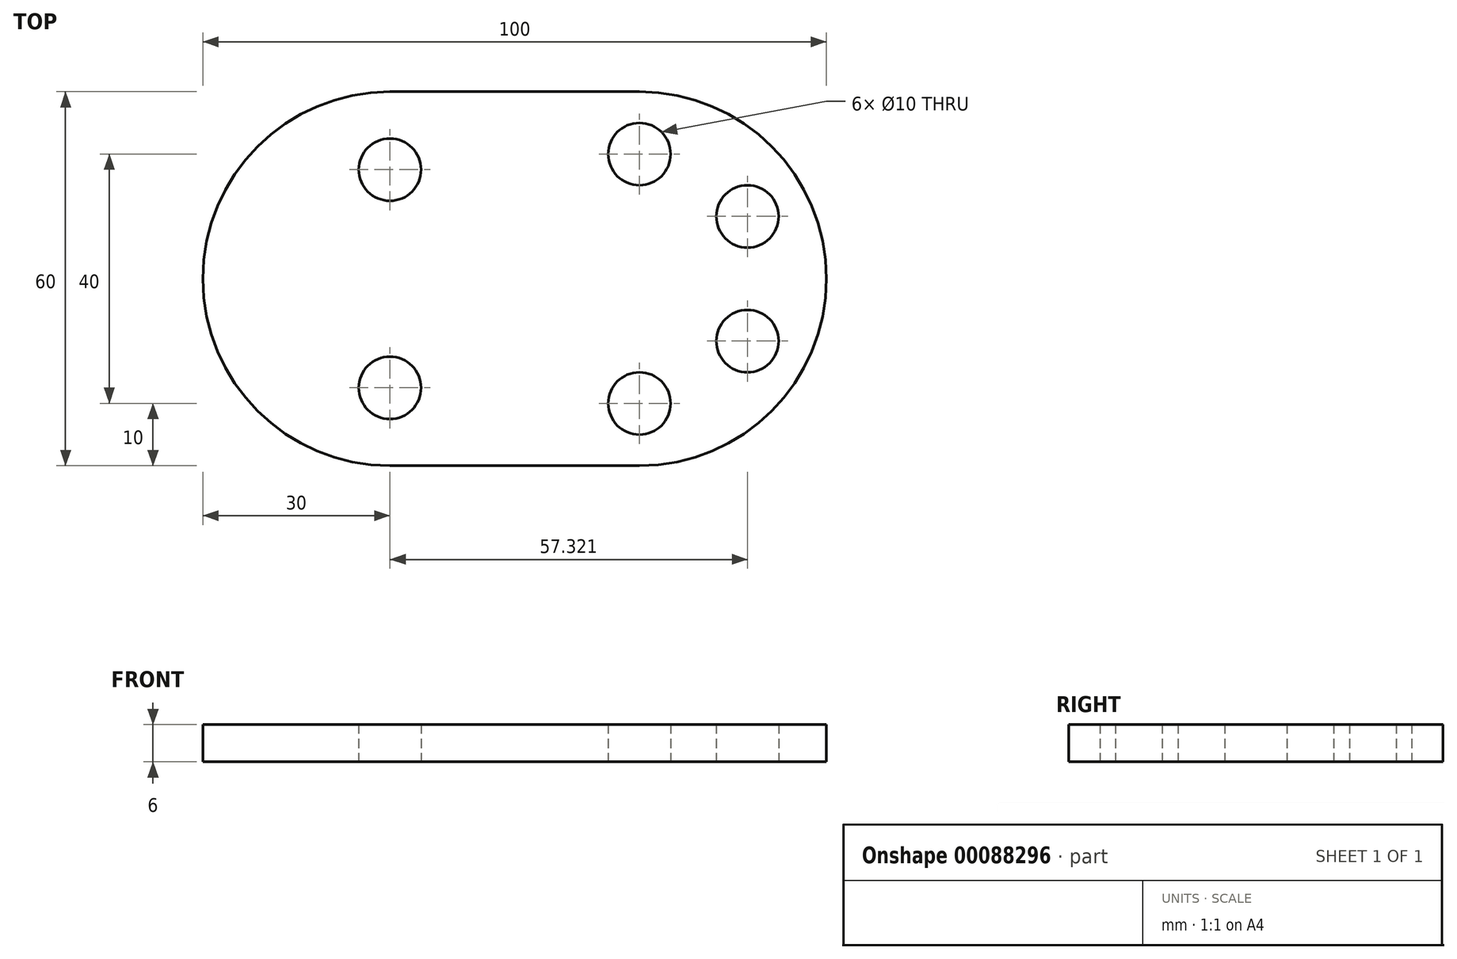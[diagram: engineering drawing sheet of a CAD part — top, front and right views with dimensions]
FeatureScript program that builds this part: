
annotation { "Feature Type Name" : "Feature", "Feature Type Description" : "" }
export const myFeature = defineFeature(function(context is Context, id is Id, definition is map)
    precondition{}
    {
        {
            var Q0;
            Q0=qCreatedBy(makeId("Top.planeOp"),FACE);
            var sketch = newSketch(context, id + "F0", { "sketchPlane" : qUnion([Q0])});
            skLineSegment(sketch, "E0.bottom", {"start": v(20, 30) * mm, "end": v(-20, 30) * mm});
            skLineSegment(sketch, "E0.top", {"start": v(20, -30) * mm, "end": v(-20, -30) * mm});
            skLineSegment(sketch, "E0.right", {"start": v(-20, 30) * mm, "end": v(-20, -30) * mm, "construction": true});
            skPoint(sketch, "E0.middle", {"position": v(0, 0) * mm});
            skArc(sketch, "E1", {"start": v(-20, 30) * mm, "mid": v(-50, 0) * mm, "end": v(-20, -30) * mm});
            skArc(sketch, "E2.MirrorCS", {"start": v(20, 30) * mm, "mid": v(50, 0) * mm, "end": v(20, -30) * mm});
            skCircle(sketch, "E3", {"center": v(-20, 17.5) * mm, "radius": 5 * mm});
            skCircle(sketch, "E4", {"center": v(-20, 0) * mm, "radius": 5 * mm, "construction": true});
            skCircle(sketch, "E5.MirrorC", {"center": v(-20, -17.5) * mm, "radius": 5 * mm});
            skLineSegment(sketch, "E6", {"start": v(-20, 12.5) * mm, "end": v(-20, 5) * mm, "construction": true});
            skLineSegment(sketch, "E7", {"start": v(-20, 22.5) * mm, "end": v(-20, 30) * mm});
            skCircle(sketch, "E8", {"center": v(20, 20) * mm, "radius": 5 * mm});
            skCircle(sketch, "E9.1.0", {"center": v(37.32, 10) * mm, "radius": 5 * mm});
            skCircle(sketch, "E9.2.0", {"center": v(37.32, -10) * mm, "radius": 5 * mm});
            skCircle(sketch, "E9.3.0", {"center": v(20, -20) * mm, "radius": 5 * mm});
            skLineSegment(sketch, "E9.anchor1", {"start": v(20, 0) * mm, "end": v(20, 20) * mm, "construction": true});
            skLineSegment(sketch, "E9.anchor2", {"start": v(20, 0) * mm, "end": v(20, -20) * mm, "construction": true});
            skSolve(sketch);
        }
        {
            var Q0;
            Q0=makeQuery(id+"F0.imprint","IMPRINT",FACE,{"disambiguationData":[TD([[makeQuery(id+"F0.imprint","IMPRINT",EDGE,{"derivedFrom":sQuery(id+"F0.wireOp",EDGE,"E0.bottom")}),1.0]])]});
            extrude(context, id + "F1", {"entities" : qUnion([Q0]), "depth" : 6 * mm});
        }
    });
